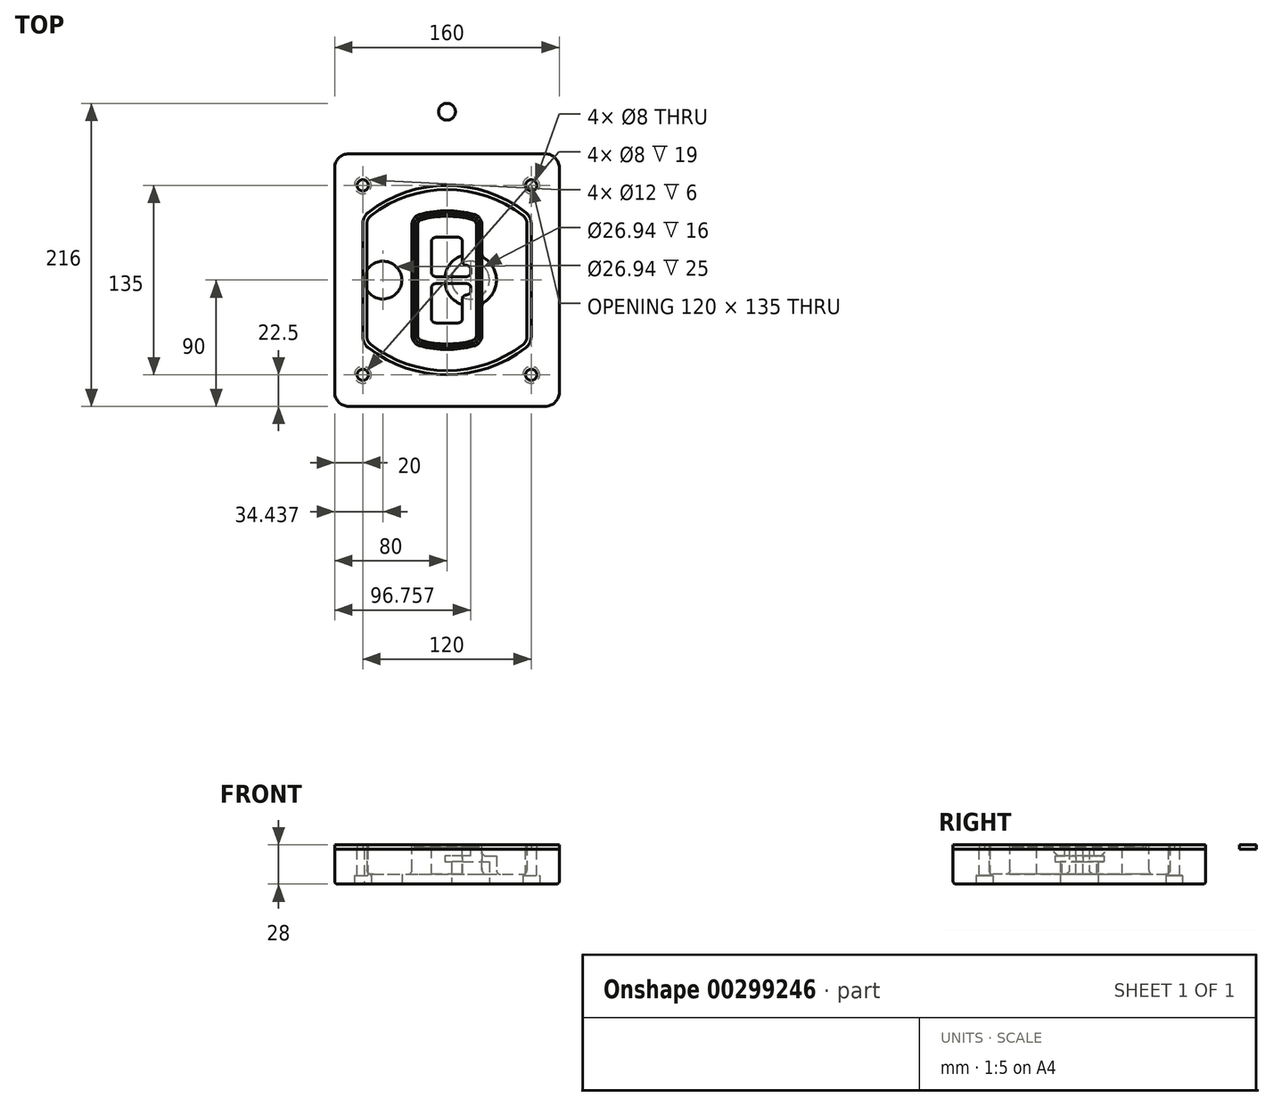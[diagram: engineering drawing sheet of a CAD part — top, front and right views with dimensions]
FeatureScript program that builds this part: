
annotation { "Feature Type Name" : "Feature", "Feature Type Description" : "" }
export const myFeature = defineFeature(function(context is Context, id is Id, definition is map)
    precondition{}
    {
        {
            var Q0;
            Q0=qCreatedBy(makeId("Top.planeOp"),FACE);
            var sketch = newSketch(context, id + "F0", { "sketchPlane" : qUnion([Q0])});
            skPoint(sketch, "E0.rect.middle", {"position": v(0, 0) * mm});
            skLineSegment(sketch, "E1.bottom", {"start": v(-70, -90) * mm, "end": v(70, -90) * mm});
            skLineSegment(sketch, "E1.top", {"start": v(-70, 90) * mm, "end": v(70, 90) * mm});
            skLineSegment(sketch, "E1.left", {"start": v(-80, -80) * mm, "end": v(-80, 80) * mm});
            skLineSegment(sketch, "E1.right", {"start": v(80, -80) * mm, "end": v(80, 80) * mm});
            skLineSegment(sketch, "E2", {"start": v(-80, 90) * mm, "end": v(80, -90) * mm, "construction": true});
            skLineSegment(sketch, "E3", {"start": v(80, 90) * mm, "end": v(-80, -90) * mm, "construction": true});
            skCircle(sketch, "E4", {"center": v(-60, 67.5) * mm, "radius": 4 * mm});
            skCircle(sketch, "E5", {"center": v(60, 67.5) * mm, "radius": 4 * mm});
            skCircle(sketch, "E6", {"center": v(60, -67.5) * mm, "radius": 4 * mm});
            skCircle(sketch, "E7", {"center": v(-60, -67.5) * mm, "radius": 4 * mm});
            skLineSegment(sketch, "E8", {"start": v(-60, 67.5) * mm, "end": v(60, 67.5) * mm, "construction": true});
            skLineSegment(sketch, "E9", {"start": v(60, 67.5) * mm, "end": v(60, -67.5) * mm, "construction": true});
            skLineSegment(sketch, "E10", {"start": v(60, -67.5) * mm, "end": v(-60, -67.5) * mm, "construction": true});
            skLineSegment(sketch, "E11", {"start": v(-60, -67.5) * mm, "end": v(-60, 67.5) * mm, "construction": true});
            skLineSegment(sketch, "E12", {"start": v(-60, 40.3) * mm, "end": v(-60, -40.3) * mm});
            skLineSegment(sketch, "E13", {"start": v(60, 40.3) * mm, "end": v(60, -40.3) * mm});
            skArc(sketch, "E14", {"start": v(56.15, 48.18) * mm, "mid": v(0, 67.5) * mm, "end": v(-56.15, 48.18) * mm});
            skArc(sketch, "E15", {"start": v(-56.15, -48.18) * mm, "mid": v(0, -67.5) * mm, "end": v(56.15, -48.18) * mm});
            skLineSegment(sketch, "E16", {"start": v(-60, 0) * mm, "end": v(60, 0) * mm, "construction": true});
            skPoint(sketch, "E17.visualSharp", {"position": v(-60, -45) * mm});
            skArc(sketch, "E17.filletArc", {"start": v(-60, -40.3) * mm, "mid": v(-58.99, -44.68) * mm, "end": v(-56.15, -48.18) * mm});
            skPoint(sketch, "E18.visualSharp", {"position": v(-60, 45) * mm});
            skArc(sketch, "E18.filletArc", {"start": v(-56.15, 48.18) * mm, "mid": v(-58.99, 44.68) * mm, "end": v(-60, 40.3) * mm});
            skPoint(sketch, "E19.visualSharp", {"position": v(60, 45) * mm});
            skArc(sketch, "E19.filletArc", {"start": v(60, 40.3) * mm, "mid": v(58.99, 44.68) * mm, "end": v(56.15, 48.18) * mm});
            skPoint(sketch, "E20.visualSharp", {"position": v(60, -45) * mm});
            skArc(sketch, "E20.filletArc", {"start": v(56.15, -48.18) * mm, "mid": v(58.99, -44.68) * mm, "end": v(60, -40.3) * mm});
            skPoint(sketch, "E21.visualSharp", {"position": v(-80, 90) * mm});
            skArc(sketch, "E21.filletArc", {"start": v(-70, 90) * mm, "mid": v(-77.07, 87.07) * mm, "end": v(-80, 80) * mm});
            skPoint(sketch, "E22.visualSharp", {"position": v(80, 90) * mm});
            skArc(sketch, "E22.filletArc", {"start": v(80, 80) * mm, "mid": v(77.07, 87.07) * mm, "end": v(70, 90) * mm});
            skPoint(sketch, "E23.visualSharp", {"position": v(80, -90) * mm});
            skArc(sketch, "E23.filletArc", {"start": v(70, -90) * mm, "mid": v(77.07, -87.07) * mm, "end": v(80, -80) * mm});
            skPoint(sketch, "E24.visualSharp", {"position": v(-80, -90) * mm});
            skArc(sketch, "E24.filletArc", {"start": v(-80, -80) * mm, "mid": v(-77.07, -87.07) * mm, "end": v(-70, -90) * mm});
            skArc(sketch, "E25.0", {"start": v(57, 40.3) * mm, "mid": v(56.3, 43.36) * mm, "end": v(54.3, 45.81) * mm});
            skLineSegment(sketch, "E25.1", {"start": v(57, 40.3) * mm, "end": v(57, -40.3) * mm});
            skArc(sketch, "E25.2", {"start": v(54.3, -45.81) * mm, "mid": v(56.3, -43.36) * mm, "end": v(57, -40.3) * mm});
            skArc(sketch, "E25.3", {"start": v(-54.3, -45.81) * mm, "mid": v(0, -64.5) * mm, "end": v(54.3, -45.81) * mm});
            skArc(sketch, "E25.4", {"start": v(-57, -40.3) * mm, "mid": v(-56.3, -43.36) * mm, "end": v(-54.3, -45.81) * mm});
            skArc(sketch, "E25.5", {"start": v(54.3, 45.81) * mm, "mid": v(0, 64.5) * mm, "end": v(-54.3, 45.81) * mm});
            skLineSegment(sketch, "E25.6", {"start": v(-57, 40.3) * mm, "end": v(-57, -40.3) * mm});
            skArc(sketch, "E25.7", {"start": v(-54.3, 45.81) * mm, "mid": v(-56.3, 43.36) * mm, "end": v(-57, 40.3) * mm});
            skArc(sketch, "E26.0", {"start": v(-58.62, 51.33) * mm, "mid": v(-62.58, 46.43) * mm, "end": v(-64, 40.3) * mm});
            skArc(sketch, "E26.1", {"start": v(58.62, 51.33) * mm, "mid": v(0, 71.5) * mm, "end": v(-58.62, 51.33) * mm});
            skArc(sketch, "E26.2", {"start": v(64, 40.3) * mm, "mid": v(62.58, 46.43) * mm, "end": v(58.62, 51.33) * mm});
            skLineSegment(sketch, "E26.3", {"start": v(64, 40.3) * mm, "end": v(64, -40.3) * mm});
            skArc(sketch, "E26.4", {"start": v(58.62, -51.33) * mm, "mid": v(62.58, -46.43) * mm, "end": v(64, -40.3) * mm});
            skLineSegment(sketch, "E26.5", {"start": v(-64, 40.3) * mm, "end": v(-64, -40.3) * mm});
            skArc(sketch, "E26.6", {"start": v(-58.62, -51.33) * mm, "mid": v(0, -71.5) * mm, "end": v(58.62, -51.33) * mm});
            skArc(sketch, "E26.7", {"start": v(-64, -40.3) * mm, "mid": v(-62.58, -46.43) * mm, "end": v(-58.62, -51.33) * mm});
            skSolve(sketch);
        }
        {
            var Q0;
            Q0=makeQuery(id+"F0.imprint","IMPRINT",FACE,{"disambiguationData":[TD([[makeQuery(id+"F0.imprint","IMPRINT",EDGE,{"derivedFrom":sQuery(id+"F0.wireOp",EDGE,"E1.bottom")}),1.0]])]});
            var Q1;
            Q1=makeQuery(id+"F0.imprint","IMPRINT",FACE,{"disambiguationData":[TD([[makeQuery(id+"F0.imprint","IMPRINT",EDGE,{"derivedFrom":sQuery(id+"F0.wireOp",EDGE,"E12")}),1.0]])]});
            var Q2;
            Q2=makeQuery(id+"F0.imprint","IMPRINT",FACE,{"disambiguationData":[TD([[makeQuery(id+"F0.imprint","IMPRINT",EDGE,{"derivedFrom":sQuery(id+"F0.wireOp",EDGE,"E25.0")}),1.0]])]});
            var Q3;
            Q3=makeQuery(id+"F0.imprint","IMPRINT",FACE,{"disambiguationData":[TD([[makeQuery(id+"F0.imprint","IMPRINT",EDGE,{"derivedFrom":sQuery(id+"F0.wireOp",EDGE,"E12")}),-1.0]])]});
            extrude(context, id + "F1", {"entities" : qUnion([Q0, Q1, Q2, Q3]), "oppositeDirection" : true, "depth" : 25 * mm});
        }
        {
            var Q0;
            Q0=makeQuery(id+"F0.imprint","IMPRINT",FACE,{"disambiguationData":[TD([[makeQuery(id+"F0.imprint","IMPRINT",EDGE,{"derivedFrom":sQuery(id+"F0.wireOp",EDGE,"E12")}),1.0]])]});
            extrude(context, id + "F2", {"entities" : qUnion([Q0]), "operationType" : NewBodyOperationType.ADD, "depth" : 3 * mm});
        }
        {
            var Q0;
            Q0=makeQuery(id+"F0.imprint","IMPRINT",FACE,{"disambiguationData":[TD([[makeQuery(id+"F0.imprint","IMPRINT",EDGE,{"derivedFrom":sQuery(id+"F0.wireOp",EDGE,"E25.0")}),1.0]])]});
            extrude(context, id + "F3", {"entities" : qUnion([Q0]), "operationType" : NewBodyOperationType.REMOVE, "oppositeDirection" : true, "depth" : 18 * mm});
        }
        {
            var Q0;
            Q0=makeQuery(id+"F2.opExtrude","CAP_FACE",FACE,{"disambiguationData":[OSD([sQuery(id+"F0.wireOp",EDGE,"E12"),sQuery(id+"F0.wireOp",EDGE,"E13"),sQuery(id+"F0.wireOp",EDGE,"E14"),sQuery(id+"F0.wireOp",EDGE,"E15"),sQuery(id+"F0.wireOp",EDGE,"E17.filletArc"),sQuery(id+"F0.wireOp",EDGE,"E18.filletArc"),sQuery(id+"F0.wireOp",EDGE,"E19.filletArc"),sQuery(id+"F0.wireOp",EDGE,"E20.filletArc"),sQuery(id+"F0.wireOp",EDGE,"E25.0"),sQuery(id+"F0.wireOp",EDGE,"E25.1"),sQuery(id+"F0.wireOp",EDGE,"E25.2"),sQuery(id+"F0.wireOp",EDGE,"E25.3"),sQuery(id+"F0.wireOp",EDGE,"E25.4"),sQuery(id+"F0.wireOp",EDGE,"E25.5"),sQuery(id+"F0.wireOp",EDGE,"E25.6"),sQuery(id+"F0.wireOp",EDGE,"E25.7")])],"isStart":false});
            var sketch = newSketch(context, id + "F4", { "sketchPlane" : qUnion([Q0])});
            skArc(sketch, "E27.0", {"start": v(-19.08, -46.97) * mm, "mid": v(0, -49.5) * mm, "end": v(19.08, -46.97) * mm});
            skArc(sketch, "E28.0", {"start": v(19.08, 46.97) * mm, "mid": v(0, 49.5) * mm, "end": v(-19.08, 46.97) * mm});
            skLineSegment(sketch, "E29", {"start": v(-25, 39.25) * mm, "end": v(-25, -39.25) * mm});
            skLineSegment(sketch, "E30", {"start": v(25, 39.25) * mm, "end": v(25, -39.25) * mm});
            skLineSegment(sketch, "E31", {"start": v(-25, 45.1) * mm, "end": v(25, 45.1) * mm, "construction": true});
            skLineSegment(sketch, "E32", {"start": v(-25, -45.1) * mm, "end": v(25, -45.1) * mm, "construction": true});
            skPoint(sketch, "E33.visualSharp", {"position": v(-25, 45.1) * mm});
            skArc(sketch, "E33.filletArc", {"start": v(-19.08, 46.97) * mm, "mid": v(-23.35, 44.11) * mm, "end": v(-25, 39.25) * mm});
            skPoint(sketch, "E34.visualSharp", {"position": v(25, 45.1) * mm});
            skArc(sketch, "E34.filletArc", {"start": v(25, 39.25) * mm, "mid": v(23.35, 44.11) * mm, "end": v(19.08, 46.97) * mm});
            skPoint(sketch, "E35.visualSharp", {"position": v(25, -45.1) * mm});
            skArc(sketch, "E35.filletArc", {"start": v(19.08, -46.97) * mm, "mid": v(23.35, -44.11) * mm, "end": v(25, -39.25) * mm});
            skPoint(sketch, "E36.visualSharp", {"position": v(-25, -45.1) * mm});
            skArc(sketch, "E36.filletArc", {"start": v(-25, -39.25) * mm, "mid": v(-23.35, -44.11) * mm, "end": v(-19.08, -46.97) * mm});
            skArc(sketch, "E37.0", {"start": v(54.3, 45.81) * mm, "mid": v(0, 64.5) * mm, "end": v(-54.3, 45.81) * mm});
            skArc(sketch, "E37.1", {"start": v(-54.3, 45.81) * mm, "mid": v(-56.3, 43.36) * mm, "end": v(-57, 40.3) * mm});
            skLineSegment(sketch, "E37.2", {"start": v(-57, 40.3) * mm, "end": v(-57, -40.3) * mm});
            skArc(sketch, "E37.3", {"start": v(-57, -40.3) * mm, "mid": v(-56.3, -43.36) * mm, "end": v(-54.3, -45.81) * mm});
            skArc(sketch, "E37.4", {"start": v(-54.3, -45.81) * mm, "mid": v(0, -64.5) * mm, "end": v(54.3, -45.81) * mm});
            skArc(sketch, "E37.5", {"start": v(54.3, -45.81) * mm, "mid": v(56.3, -43.36) * mm, "end": v(57, -40.3) * mm});
            skLineSegment(sketch, "E37.6", {"start": v(57, 40.3) * mm, "end": v(57, -40.3) * mm});
            skArc(sketch, "E37.7", {"start": v(57, 40.3) * mm, "mid": v(56.3, 43.36) * mm, "end": v(54.3, 45.81) * mm});
            skLineSegment(sketch, "E38.0", {"start": v(23, 39.25) * mm, "end": v(23, -39.25) * mm});
            skArc(sketch, "E38.1", {"start": v(18.56, -45.04) * mm, "mid": v(21.76, -42.9) * mm, "end": v(23, -39.25) * mm});
            skArc(sketch, "E38.2", {"start": v(-18.56, -45.04) * mm, "mid": v(0, -47.5) * mm, "end": v(18.56, -45.04) * mm});
            skArc(sketch, "E38.3", {"start": v(-23, -39.25) * mm, "mid": v(-21.76, -42.9) * mm, "end": v(-18.56, -45.04) * mm});
            skLineSegment(sketch, "E38.4", {"start": v(-23, 39.25) * mm, "end": v(-23, -39.25) * mm});
            skArc(sketch, "E38.5", {"start": v(23, 39.25) * mm, "mid": v(21.76, 42.9) * mm, "end": v(18.56, 45.04) * mm});
            skArc(sketch, "E38.6", {"start": v(-18.56, 45.04) * mm, "mid": v(-21.76, 42.9) * mm, "end": v(-23, 39.25) * mm});
            skArc(sketch, "E38.7", {"start": v(18.56, 45.04) * mm, "mid": v(0, 47.5) * mm, "end": v(-18.56, 45.04) * mm});
            skArc(sketch, "E39.0", {"start": v(21, 39.25) * mm, "mid": v(20.18, 41.68) * mm, "end": v(18.04, 43.1) * mm});
            skLineSegment(sketch, "E39.1", {"start": v(21, 39.25) * mm, "end": v(21, -39.25) * mm});
            skArc(sketch, "E39.2", {"start": v(18.04, -43.1) * mm, "mid": v(20.18, -41.68) * mm, "end": v(21, -39.25) * mm});
            skArc(sketch, "E39.3", {"start": v(-18.04, -43.1) * mm, "mid": v(0, -45.5) * mm, "end": v(18.04, -43.1) * mm});
            skArc(sketch, "E39.4", {"start": v(-21, -39.25) * mm, "mid": v(-20.18, -41.68) * mm, "end": v(-18.04, -43.1) * mm});
            skArc(sketch, "E39.5", {"start": v(18.04, 43.1) * mm, "mid": v(0, 45.5) * mm, "end": v(-18.04, 43.1) * mm});
            skLineSegment(sketch, "E39.6", {"start": v(-21, 39.25) * mm, "end": v(-21, -39.25) * mm});
            skArc(sketch, "E39.7", {"start": v(-18.04, 43.1) * mm, "mid": v(-20.18, 41.68) * mm, "end": v(-21, 39.25) * mm});
            skLineSegment(sketch, "E40", {"start": v(-25, 0) * mm, "end": v(25, 0) * mm, "construction": true});
            skLineSegment(sketch, "E41", {"start": v(-11, 5.5) * mm, "end": v(-11, 27.5) * mm});
            skLineSegment(sketch, "E42", {"start": v(-8, 30.5) * mm, "end": v(8, 30.5) * mm});
            skLineSegment(sketch, "E43", {"start": v(11, 27.5) * mm, "end": v(11, 13.5) * mm});
            skLineSegment(sketch, "E44", {"start": v(14, 10.5) * mm, "end": v(14, 10.5) * mm});
            skLineSegment(sketch, "E45", {"start": v(17, 7.5) * mm, "end": v(17, 5.5) * mm});
            skLineSegment(sketch, "E46", {"start": v(14, 2.5) * mm, "end": v(-8, 2.5) * mm});
            skPoint(sketch, "E47.visualSharp", {"position": v(-11, 30.5) * mm});
            skArc(sketch, "E47.filletArc", {"start": v(-8, 30.5) * mm, "mid": v(-10.12, 29.62) * mm, "end": v(-11, 27.5) * mm});
            skPoint(sketch, "E48.visualSharp", {"position": v(11, 30.5) * mm});
            skArc(sketch, "E48.filletArc", {"start": v(11, 27.5) * mm, "mid": v(10.12, 29.62) * mm, "end": v(8, 30.5) * mm});
            skPoint(sketch, "E49.visualSharp", {"position": v(11, 10.5) * mm});
            skArc(sketch, "E49.filletArc", {"start": v(11, 13.5) * mm, "mid": v(11.88, 11.38) * mm, "end": v(14, 10.5) * mm});
            skPoint(sketch, "E50.visualSharp", {"position": v(17, 10.5) * mm});
            skArc(sketch, "E50.filletArc", {"start": v(17, 7.5) * mm, "mid": v(16.12, 9.62) * mm, "end": v(14, 10.5) * mm});
            skPoint(sketch, "E51.visualSharp", {"position": v(17, 2.5) * mm});
            skArc(sketch, "E51.filletArc", {"start": v(14, 2.5) * mm, "mid": v(16.12, 3.38) * mm, "end": v(17, 5.5) * mm});
            skPoint(sketch, "E52.visualSharp", {"position": v(-11, 2.5) * mm});
            skArc(sketch, "E52.filletArc", {"start": v(-11, 5.5) * mm, "mid": v(-10.12, 3.38) * mm, "end": v(-8, 2.5) * mm});
            skLineSegment(sketch, "E53.0.MirrorCS", {"start": v(14, -2.5) * mm, "end": v(-8, -2.5) * mm});
            skArc(sketch, "E54.0.MirrorCS", {"start": v(-11, -5.5) * mm, "mid": v(-10.12, -3.38) * mm, "end": v(-8, -2.5) * mm});
            skLineSegment(sketch, "E55.0.MirrorCS", {"start": v(-11, -5.5) * mm, "end": v(-11, -27.5) * mm});
            skArc(sketch, "E56.0.MirrorCS", {"start": v(-8, -30.5) * mm, "mid": v(-10.12, -29.62) * mm, "end": v(-11, -27.5) * mm});
            skLineSegment(sketch, "E57.0.MirrorCS", {"start": v(-8, -30.5) * mm, "end": v(8, -30.5) * mm});
            skArc(sketch, "E58.0.MirrorCS", {"start": v(11, -27.5) * mm, "mid": v(10.12, -29.62) * mm, "end": v(8, -30.5) * mm});
            skLineSegment(sketch, "E59.0.MirrorCS", {"start": v(11, -27.5) * mm, "end": v(11, -13.5) * mm});
            skArc(sketch, "E60.0.MirrorCS", {"start": v(11, -13.5) * mm, "mid": v(11.88, -11.38) * mm, "end": v(14, -10.5) * mm});
            skArc(sketch, "E61.0.MirrorCS", {"start": v(17, -7.5) * mm, "mid": v(16.12, -9.62) * mm, "end": v(14, -10.5) * mm});
            skLineSegment(sketch, "E62.0.MirrorCS", {"start": v(17, -7.5) * mm, "end": v(17, -5.5) * mm});
            skArc(sketch, "E63.0.MirrorCS", {"start": v(14, -2.5) * mm, "mid": v(16.12, -3.38) * mm, "end": v(17, -5.5) * mm});
            skSolve(sketch);
        }
        {
            var Q0;
            Q0=makeQuery(id+"F4.imprint","IMPRINT",FACE,{"disambiguationData":[TD([[makeQuery(id+"F4.imprint","IMPRINT",EDGE,{"derivedFrom":sQuery(id+"F4.wireOp",EDGE,"E27.0")}),1.0]])]});
            var Q1;
            Q1=makeQuery(id+"F4.imprint","IMPRINT",FACE,{"disambiguationData":[TD([[makeQuery(id+"F4.imprint","IMPRINT",EDGE,{"derivedFrom":sQuery(id+"F4.wireOp",EDGE,"E38.0")}),-1.0]])]});
            var Q2;
            Q2=makeQuery(id+"F4.imprint","IMPRINT",FACE,{"disambiguationData":[TD([[makeQuery(id+"F4.imprint","IMPRINT",EDGE,{"derivedFrom":sQuery(id+"F4.wireOp",EDGE,"E39.0")}),1.0]])]});
            extrude(context, id + "F5", {"entities" : qUnion([Q0, Q1, Q2]), "operationType" : NewBodyOperationType.ADD, "endBound" : BoundingType.UP_TO_NEXT, "oppositeDirection" : true, "depth" : 25 * mm});
        }
        {
            var Q0;
            Q0=makeQuery(id+"F4.imprint","IMPRINT",FACE,{"disambiguationData":[TD([[makeQuery(id+"F4.imprint","IMPRINT",EDGE,{"derivedFrom":sQuery(id+"F4.wireOp",EDGE,"E38.0")}),-1.0]])]});
            extrude(context, id + "F6", {"entities" : qUnion([Q0]), "operationType" : NewBodyOperationType.REMOVE, "oppositeDirection" : true, "depth" : 2 * mm});
        }
        {
            var Q0;
            Q0=makeQuery(id+"F1.opExtrude","CAP_FACE",FACE,{"disambiguationData":[OSD([sQuery(id+"F0.wireOp",EDGE,"E1.bottom"),sQuery(id+"F0.wireOp",EDGE,"E1.top"),sQuery(id+"F0.wireOp",EDGE,"E1.left"),sQuery(id+"F0.wireOp",EDGE,"E1.right"),sQuery(id+"F0.wireOp",EDGE,"E4"),sQuery(id+"F0.wireOp",EDGE,"E5"),sQuery(id+"F0.wireOp",EDGE,"E6"),sQuery(id+"F0.wireOp",EDGE,"E7"),sQuery(id+"F0.wireOp",EDGE,"E21.filletArc"),sQuery(id+"F0.wireOp",EDGE,"E22.filletArc"),sQuery(id+"F0.wireOp",EDGE,"E23.filletArc"),sQuery(id+"F0.wireOp",EDGE,"E24.filletArc")])],"isStart":false});
            var sketch = newSketch(context, id + "F7", { "sketchPlane" : qUnion([Q0])});
            skCircle(sketch, "E64", {"center": v(16.76, 0) * mm, "radius": 13.47 * mm});
            skCircle(sketch, "E65", {"center": v(-45.56, 0) * mm, "radius": 13.47 * mm});
            skLineSegment(sketch, "E66", {"start": v(80, 0) * mm, "end": v(-80, 0) * mm});
            skCircle(sketch, "E67", {"center": v(16.76, 0) * mm, "radius": 18.47 * mm});
            skCircle(sketch, "E68", {"center": v(60, -67.5) * mm, "radius": 6 * mm});
            skCircle(sketch, "E69", {"center": v(-60, -67.5) * mm, "radius": 6 * mm});
            skCircle(sketch, "E70", {"center": v(-60, 67.5) * mm, "radius": 6 * mm});
            skCircle(sketch, "E71", {"center": v(60, 67.5) * mm, "radius": 6 * mm});
            skSolve(sketch);
        }
        {
            var Q0;
            {var subQ1=sQuery(id+"F7.wireOp",EDGE,"E66");var subQ4=sQuery(id+"F7.wireOp",EDGE,"E64");var subQ6=makeQuery(id+"F7.imprint","INTERSECT",VERTEX,{"disambiguationData":[OD(0.0)],"derivedFrom":[subQ4,subQ1]});Q0=makeQuery(id+"F7.imprint","IMPRINT",FACE,{"disambiguationData":[TD([[makeQuery(id+"F7.imprint","IMPRINT",EDGE,{"disambiguationData":[TD([[subQ6,-1.0]])],"derivedFrom":subQ4}),-1.0]])]});}
            var Q1;
            {var subQ0=sQuery(id+"F7.wireOp",EDGE,"E66");var subQ1=sQuery(id+"F7.wireOp",EDGE,"E64");var subQ3=makeQuery(id+"F7.imprint","INTERSECT",VERTEX,{"disambiguationData":[OD(0.0)],"derivedFrom":[subQ1,subQ0]});Q1=makeQuery(id+"F7.imprint","IMPRINT",FACE,{"disambiguationData":[TD([[makeQuery(id+"F7.imprint","IMPRINT",EDGE,{"disambiguationData":[TD([[subQ3,-1.0]])],"derivedFrom":subQ1}),1.0]])]});}
            var Q2;
            {var subQ0=sQuery(id+"F7.wireOp",EDGE,"E66");var subQ1=sQuery(id+"F7.wireOp",EDGE,"E64");var subQ3=makeQuery(id+"F7.imprint","INTERSECT",VERTEX,{"disambiguationData":[OD(0.0)],"derivedFrom":[subQ1,subQ0]});Q2=makeQuery(id+"F7.imprint","IMPRINT",FACE,{"disambiguationData":[TD([[makeQuery(id+"F7.imprint","IMPRINT",EDGE,{"disambiguationData":[TD([[subQ3,1.0]])],"derivedFrom":subQ1}),1.0]])]});}
            var Q3;
            {var subQ1=sQuery(id+"F7.wireOp",EDGE,"E66");var subQ4=sQuery(id+"F7.wireOp",EDGE,"E64");var subQ6=makeQuery(id+"F7.imprint","INTERSECT",VERTEX,{"disambiguationData":[OD(0.0)],"derivedFrom":[subQ4,subQ1]});Q3=makeQuery(id+"F7.imprint","IMPRINT",FACE,{"disambiguationData":[TD([[makeQuery(id+"F7.imprint","IMPRINT",EDGE,{"disambiguationData":[TD([[subQ6,1.0]])],"derivedFrom":subQ4}),-1.0]])]});}
            extrude(context, id + "F8", {"entities" : qUnion([Q0, Q1, Q2, Q3]), "operationType" : NewBodyOperationType.ADD, "oppositeDirection" : true, "depth" : 20 * mm});
        }
        {
            var Q0;
            {var subQ0=sQuery(id+"F7.wireOp",EDGE,"E66");var subQ1=sQuery(id+"F7.wireOp",EDGE,"E64");var subQ3=makeQuery(id+"F7.imprint","INTERSECT",VERTEX,{"disambiguationData":[OD(0.0)],"derivedFrom":[subQ1,subQ0]});Q0=makeQuery(id+"F7.imprint","IMPRINT",FACE,{"disambiguationData":[TD([[makeQuery(id+"F7.imprint","IMPRINT",EDGE,{"disambiguationData":[TD([[subQ3,-1.0]])],"derivedFrom":subQ1}),1.0]])]});}
            var Q1;
            {var subQ0=sQuery(id+"F7.wireOp",EDGE,"E66");var subQ1=sQuery(id+"F7.wireOp",EDGE,"E64");var subQ3=makeQuery(id+"F7.imprint","INTERSECT",VERTEX,{"disambiguationData":[OD(0.0)],"derivedFrom":[subQ1,subQ0]});Q1=makeQuery(id+"F7.imprint","IMPRINT",FACE,{"disambiguationData":[TD([[makeQuery(id+"F7.imprint","IMPRINT",EDGE,{"disambiguationData":[TD([[subQ3,1.0]])],"derivedFrom":subQ1}),1.0]])]});}
            extrude(context, id + "F9", {"entities" : qUnion([Q0, Q1]), "operationType" : NewBodyOperationType.REMOVE, "oppositeDirection" : true, "depth" : 16 * mm});
        }
        {
            var Q0;
            {var subQ0=sQuery(id+"F7.wireOp",EDGE,"E66");var subQ1=sQuery(id+"F7.wireOp",EDGE,"E65");var subQ3=makeQuery(id+"F7.imprint","INTERSECT",VERTEX,{"disambiguationData":[OD(0.0)],"derivedFrom":[subQ1,subQ0]});Q0=makeQuery(id+"F7.imprint","IMPRINT",FACE,{"disambiguationData":[TD([[makeQuery(id+"F7.imprint","IMPRINT",EDGE,{"disambiguationData":[TD([[subQ3,-1.0]])],"derivedFrom":subQ1}),1.0]])]});}
            var Q1;
            {var subQ0=sQuery(id+"F7.wireOp",EDGE,"E66");var subQ1=sQuery(id+"F7.wireOp",EDGE,"E65");var subQ3=makeQuery(id+"F7.imprint","INTERSECT",VERTEX,{"disambiguationData":[OD(0.0)],"derivedFrom":[subQ1,subQ0]});Q1=makeQuery(id+"F7.imprint","IMPRINT",FACE,{"disambiguationData":[TD([[makeQuery(id+"F7.imprint","IMPRINT",EDGE,{"disambiguationData":[TD([[subQ3,1.0]])],"derivedFrom":subQ1}),1.0]])]});}
            extrude(context, id + "F10", {"entities" : qUnion([Q0, Q1]), "operationType" : NewBodyOperationType.REMOVE, "oppositeDirection" : true, "depth" : 25 * mm});
        }
        {
            var Q0;
            Q0=makeQuery(id+"F7.imprint","IMPRINT",FACE,{"disambiguationData":[TD([[makeQuery(id+"F7.imprint","IMPRINT",EDGE,{"derivedFrom":sQuery(id+"F7.wireOp",EDGE,"E68")}),1.0]])]});
            var Q1;
            Q1=makeQuery(id+"F7.imprint","IMPRINT",FACE,{"disambiguationData":[TD([[makeQuery(id+"F7.imprint","IMPRINT",EDGE,{"derivedFrom":makeQuery(id+"F1.opExtrude","CAP_EDGE",EDGE,{"disambiguationData":[OSD([sQuery(id+"F0.wireOp",EDGE,"E5")])],"isStart":false})}),-1.0]])]});
            var Q2;
            Q2=makeQuery(id+"F7.imprint","IMPRINT",FACE,{"disambiguationData":[TD([[makeQuery(id+"F7.imprint","IMPRINT",EDGE,{"derivedFrom":sQuery(id+"F7.wireOp",EDGE,"E69")}),1.0]])]});
            var Q3;
            Q3=makeQuery(id+"F7.imprint","IMPRINT",FACE,{"disambiguationData":[TD([[makeQuery(id+"F7.imprint","IMPRINT",EDGE,{"derivedFrom":makeQuery(id+"F1.opExtrude","CAP_EDGE",EDGE,{"disambiguationData":[OSD([sQuery(id+"F0.wireOp",EDGE,"E4")])],"isStart":false})}),-1.0]])]});
            var Q4;
            Q4=makeQuery(id+"F7.imprint","IMPRINT",FACE,{"disambiguationData":[TD([[makeQuery(id+"F7.imprint","IMPRINT",EDGE,{"derivedFrom":sQuery(id+"F7.wireOp",EDGE,"E70")}),1.0]])]});
            var Q5;
            Q5=makeQuery(id+"F7.imprint","IMPRINT",FACE,{"disambiguationData":[TD([[makeQuery(id+"F7.imprint","IMPRINT",EDGE,{"derivedFrom":makeQuery(id+"F1.opExtrude","CAP_EDGE",EDGE,{"disambiguationData":[OSD([sQuery(id+"F0.wireOp",EDGE,"E7")])],"isStart":false})}),-1.0]])]});
            var Q6;
            Q6=makeQuery(id+"F7.imprint","IMPRINT",FACE,{"disambiguationData":[TD([[makeQuery(id+"F7.imprint","IMPRINT",EDGE,{"derivedFrom":sQuery(id+"F7.wireOp",EDGE,"E71")}),1.0]])]});
            var Q7;
            Q7=makeQuery(id+"F7.imprint","IMPRINT",FACE,{"disambiguationData":[TD([[makeQuery(id+"F7.imprint","IMPRINT",EDGE,{"derivedFrom":makeQuery(id+"F1.opExtrude","CAP_EDGE",EDGE,{"disambiguationData":[OSD([sQuery(id+"F0.wireOp",EDGE,"E6")])],"isStart":false})}),-1.0]])]});
            extrude(context, id + "F11", {"entities" : qUnion([Q0, Q1, Q2, Q3, Q4, Q5, Q6, Q7]), "operationType" : NewBodyOperationType.REMOVE, "oppositeDirection" : true, "depth" : 6 * mm});
        }
        {
            var Q0;
            Q0=makeQuery(id+"F9.boolean.opBoolean","COPY",FACE,{"derivedFrom":makeQuery(id+"F9.opExtrude","CAP_FACE",FACE,{"disambiguationData":[OSD([sQuery(id+"F7.wireOp",EDGE,"E64")])],"isStart":false})});
            var sketch = newSketch(context, id + "F12", { "sketchPlane" : qUnion([Q0])});
            skArc(sketch, "E72.0", {"start": v(11, 17.55) * mm, "mid": v(2.57, 11.82) * mm, "end": v(-1.54, 2.5) * mm});
            skArc(sketch, "E72.1", {"start": v(-1.54, -2.5) * mm, "mid": v(2.57, -11.82) * mm, "end": v(11, -17.55) * mm});
            skLineSegment(sketch, "E73", {"start": v(-1.54, -2.5) * mm, "end": v(14, -2.5) * mm});
            skLineSegment(sketch, "E74.0", {"start": v(14, 2.5) * mm, "end": v(-1.54, 2.5) * mm});
            skArc(sketch, "E74.1", {"start": v(14, 2.5) * mm, "mid": v(16.12, 3.38) * mm, "end": v(17, 5.5) * mm});
            skLineSegment(sketch, "E74.2", {"start": v(17, 7.5) * mm, "end": v(17, 5.5) * mm});
            skArc(sketch, "E74.3", {"start": v(17, 7.5) * mm, "mid": v(16.12, 9.62) * mm, "end": v(14, 10.5) * mm});
            skArc(sketch, "E74.4", {"start": v(11, 13.5) * mm, "mid": v(11.88, 11.38) * mm, "end": v(14, 10.5) * mm});
            skLineSegment(sketch, "E74.5", {"start": v(11, 17.55) * mm, "end": v(11, 13.5) * mm});
            skLineSegment(sketch, "E74.7", {"start": v(14, -2.5) * mm, "end": v(-1.54, -2.5) * mm});
            skArc(sketch, "E74.8", {"start": v(14, -2.5) * mm, "mid": v(16.12, -3.38) * mm, "end": v(17, -5.5) * mm});
            skLineSegment(sketch, "E74.9", {"start": v(17, -7.5) * mm, "end": v(17, -5.5) * mm});
            skArc(sketch, "E74.10", {"start": v(17, -7.5) * mm, "mid": v(16.12, -9.62) * mm, "end": v(14, -10.5) * mm});
            skArc(sketch, "E74.11", {"start": v(11, -13.5) * mm, "mid": v(11.88, -11.38) * mm, "end": v(14, -10.5) * mm});
            skLineSegment(sketch, "E74.12", {"start": v(11, -17.55) * mm, "end": v(11, -13.5) * mm});
            skPoint(sketch, "E75.orphan", {"position": v(11, -27.5) * mm});
            skPoint(sketch, "E76.orphan", {"position": v(-8, -2.5) * mm});
            skPoint(sketch, "E77.orphan", {"position": v(-8, 2.5) * mm});
            skPoint(sketch, "E78.orphan", {"position": v(11, 27.5) * mm});
            skSolve(sketch);
        }
        {
            var Q0;
            {var subQ7=sQuery(id+"F12.wireOp",EDGE,"E72.0");var subQ14=sQuery(id+"F12.wireOp",EDGE,"E72.1");var subQ16=sQuery(id+"F12.wireOp",EDGE,"E74.1");var subQ18=sQuery(id+"F12.wireOp",EDGE,"E74.8");Q0=qUnion([makeQuery(id+"F12.imprint","IMPRINT",FACE,{"disambiguationData":[TD([[makeQuery(id+"F12.imprint","IMPRINT",EDGE,{"derivedFrom":subQ7}),1.0]])]}),makeQuery(id+"F12.imprint","IMPRINT",FACE,{"disambiguationData":[TD([[makeQuery(id+"F12.imprint","IMPRINT",EDGE,{"derivedFrom":subQ14}),1.0]])]}),makeQuery(id+"F12.imprint","IMPRINT",FACE,{"disambiguationData":[TD([[makeQuery(id+"F12.imprint","IMPRINT",EDGE,{"derivedFrom":subQ16}),1.0]])]}),makeQuery(id+"F12.imprint","IMPRINT",FACE,{"disambiguationData":[TD([[makeQuery(id+"F12.imprint","IMPRINT",EDGE,{"derivedFrom":subQ18}),-1.0]])]})]);}
            var Q1;
            Q1=makeQuery(id+"F5.boolean.opBoolean","SPLIT",FACE,{"disambiguationData":[TD([makeQuery(id+"F5.opExtrude","SWEPT_FACE",FACE,{"disambiguationData":[OSD([sQuery(id+"F4.wireOp",EDGE,"E41")])]})])],"derivedFrom":makeQuery(id+"F3.boolean.opBoolean","COPY",FACE,{"derivedFrom":makeQuery(id+"F3.opExtrude","CAP_FACE",FACE,{"disambiguationData":[OSD([sQuery(id+"F0.wireOp",EDGE,"E25.0"),sQuery(id+"F0.wireOp",EDGE,"E25.1"),sQuery(id+"F0.wireOp",EDGE,"E25.2"),sQuery(id+"F0.wireOp",EDGE,"E25.3"),sQuery(id+"F0.wireOp",EDGE,"E25.4"),sQuery(id+"F0.wireOp",EDGE,"E25.5"),sQuery(id+"F0.wireOp",EDGE,"E25.6"),sQuery(id+"F0.wireOp",EDGE,"E25.7")])],"isStart":false})})});
            extrude(context, id + "F13", {"entities" : qUnion([Q0]), "operationType" : NewBodyOperationType.REMOVE, "endBound" : BoundingType.UP_TO_SURFACE, "endBoundEntityFace" : qUnion([Q1]), "depth" : 25 * mm});
        }
        {
            var Q0;
            Q0=makeQuery(id+"F3.boolean.opBoolean","COPY",EDGE,{"derivedFrom":makeQuery(id+"F3.opExtrude","CAP_EDGE",EDGE,{"disambiguationData":[OSD([sQuery(id+"F0.wireOp",EDGE,"E25.6")])],"isStart":false})});
            var Q1;
            Q1=makeQuery(id+"F8.boolean.opBoolean","INTERSECT",EDGE,{"derivedFrom":[makeQuery(id+"F5.opExtrude","SWEPT_FACE",FACE,{"disambiguationData":[OSD([sQuery(id+"F4.wireOp",EDGE,"E30")])]}),makeQuery(id+"F8.opExtrude","CAP_FACE",FACE,{"disambiguationData":[OSD([sQuery(id+"F7.wireOp",EDGE,"E67")])],"isStart":false})]});
            var Q2;
            Q2=makeQuery(id+"F8.boolean.opBoolean","INTERSECT",EDGE,{"disambiguationData":[OD(1.0)],"derivedFrom":[makeQuery(id+"F5.opExtrude","SWEPT_FACE",FACE,{"disambiguationData":[OSD([sQuery(id+"F4.wireOp",EDGE,"E30")])]}),makeQuery(id+"F8.opExtrude","SWEPT_FACE",FACE,{"disambiguationData":[OSD([sQuery(id+"F7.wireOp",EDGE,"E67")])]})]});
            var Q3;
            {var subQ0=sQuery(id+"F4.wireOp",EDGE,"E30");Q3=makeQuery(id+"F8.boolean.opBoolean","SPLIT",EDGE,{"disambiguationData":[TD([makeQuery(id+"F5.opExtrude","SWEPT_FACE",FACE,{"disambiguationData":[OSD([sQuery(id+"F4.wireOp",EDGE,"E35.filletArc")])]})])],"derivedFrom":makeQuery(id+"F5.opExtrude","CAP_EDGE",EDGE,{"disambiguationData":[OSD([subQ0])],"isStart":false})});}
            var Q4;
            {var subQ0=sQuery(id+"F0.wireOp",EDGE,"E25.7");var subQ1=sQuery(id+"F0.wireOp",EDGE,"E25.1");var subQ2=sQuery(id+"F0.wireOp",EDGE,"E25.6");var subQ3=sQuery(id+"F0.wireOp",EDGE,"E25.5");var subQ4=sQuery(id+"F0.wireOp",EDGE,"E25.4");var subQ5=sQuery(id+"F0.wireOp",EDGE,"E25.0");var subQ6=sQuery(id+"F0.wireOp",EDGE,"E25.2");var subQ7=sQuery(id+"F0.wireOp",EDGE,"E25.3");Q4=makeQuery(id+"F8.boolean.opBoolean","INTERSECT",EDGE,{"derivedFrom":[makeQuery(id+"F5.boolean.opBoolean","SPLIT",FACE,{"disambiguationData":[TD([makeQuery(id+"F2.opExtrude","SWEPT_FACE",FACE,{"disambiguationData":[OSD([subQ5])]})])],"derivedFrom":makeQuery(id+"F3.boolean.opBoolean","COPY",FACE,{"derivedFrom":makeQuery(id+"F3.opExtrude","CAP_FACE",FACE,{"disambiguationData":[OSD([subQ5,subQ1,subQ6,subQ7,subQ4,subQ3,subQ2,subQ0])],"isStart":false})})}),makeQuery(id+"F8.opExtrude","SWEPT_FACE",FACE,{"disambiguationData":[OSD([sQuery(id+"F7.wireOp",EDGE,"E67")])]})]});}
            var Q5;
            Q5=makeQuery(id+"F8.boolean.opBoolean","INTERSECT",EDGE,{"disambiguationData":[OD(0.0)],"derivedFrom":[makeQuery(id+"F5.opExtrude","SWEPT_FACE",FACE,{"disambiguationData":[OSD([sQuery(id+"F4.wireOp",EDGE,"E30")])]}),makeQuery(id+"F8.opExtrude","SWEPT_FACE",FACE,{"disambiguationData":[OSD([sQuery(id+"F7.wireOp",EDGE,"E67")])]})]});
            fillet(context, id + "F14", {"entities" : qUnion([Q0, Q1, Q2, Q3, Q4, Q5]), "radius" : 3 * mm, "tangentPropagation" : true, "allowEdgeOverflow" : false});
        }
        {
            var Q0;
            Q0=makeQuery(id+"F1.opExtrude","CAP_EDGE",EDGE,{"disambiguationData":[OSD([sQuery(id+"F0.wireOp",EDGE,"E1.bottom")])],"isStart":false});
            fillet(context, id + "F15", {"entities" : qUnion([Q0]), "radius" : 2 * mm, "tangentPropagation" : true, "allowEdgeOverflow" : false});
        }
        {
            var Q0;
            {var subQ0=sQuery(id+"F0.wireOp",EDGE,"E21.filletArc");var subQ1=sQuery(id+"F0.wireOp",EDGE,"E7");var subQ2=sQuery(id+"F0.wireOp",EDGE,"E6");var subQ3=sQuery(id+"F0.wireOp",EDGE,"E5");var subQ4=sQuery(id+"F0.wireOp",EDGE,"E4");var subQ5=sQuery(id+"F0.wireOp",EDGE,"E22.filletArc");var subQ6=sQuery(id+"F0.wireOp",EDGE,"E1.bottom");var subQ7=sQuery(id+"F0.wireOp",EDGE,"E1.right");var subQ8=sQuery(id+"F0.wireOp",EDGE,"E1.top");var subQ9=sQuery(id+"F0.wireOp",EDGE,"E1.left");var subQ10=sQuery(id+"F0.wireOp",EDGE,"E23.filletArc");var subQ11=sQuery(id+"F0.wireOp",EDGE,"E24.filletArc");Q0=makeQuery(id+"F2.boolean.opBoolean","SPLIT",FACE,{"disambiguationData":[TD([makeQuery(id+"F1.opExtrude","SWEPT_FACE",FACE,{"disambiguationData":[OSD([subQ6])]})])],"derivedFrom":makeQuery(id+"F1.opExtrude","CAP_FACE",FACE,{"disambiguationData":[OSD([subQ6,subQ8,subQ9,subQ7,subQ4,subQ3,subQ2,subQ1,subQ0,subQ5,subQ10,subQ11])],"isStart":true})});}
            var sketch = newSketch(context, id + "F16", { "sketchPlane" : qUnion([Q0])});
            skLineSegment(sketch, "E79", {"start": v(0, 90) * mm, "end": v(0, 90) * mm});
            skLineSegment(sketch, "E80", {"start": v(0, 90) * mm, "end": v(0, 120) * mm, "construction": true});
            skCircle(sketch, "E81", {"center": v(0, 120) * mm, "radius": 6 * mm});
            skArc(sketch, "E82", {"start": v(15, 120) * mm, "mid": v(0, 135) * mm, "end": v(-15, 120) * mm});
            skLineSegment(sketch, "E83", {"start": v(-15, 120) * mm, "end": v(-15, 108) * mm});
            skLineSegment(sketch, "E84", {"start": v(-15, 108) * mm, "end": v(-33, 90) * mm});
            skLineSegment(sketch, "E85", {"start": v(15, 120) * mm, "end": v(15, 108) * mm});
            skLineSegment(sketch, "E86", {"start": v(15, 108) * mm, "end": v(33, 90) * mm});
            skLineSegment(sketch, "E87", {"start": v(-80, 0) * mm, "end": v(80, 0) * mm, "construction": true});
            skLineSegment(sketch, "E88.MirrorCS", {"start": v(15, -108) * mm, "end": v(33, -90) * mm});
            skArc(sketch, "E89.MirrorCS", {"start": v(15, -120) * mm, "mid": v(0, -135) * mm, "end": v(-15, -120) * mm});
            skLineSegment(sketch, "E90.MirrorCS", {"start": v(-15, -120) * mm, "end": v(-15, -108) * mm});
            skLineSegment(sketch, "E91.MirrorCS", {"start": v(-15, -108) * mm, "end": v(-33, -90) * mm});
            skLineSegment(sketch, "E92.MirrorCS", {"start": v(15, -120) * mm, "end": v(15, -108) * mm});
            skCircle(sketch, "E93.MirrorC", {"center": v(0, -120) * mm, "radius": 6 * mm});
            skLineSegment(sketch, "E94.MirrorCS", {"start": v(0, -90) * mm, "end": v(0, -120) * mm, "construction": true});
            skSolve(sketch);
        }
        {
            var Q0;
            Q0=makeQuery(id+"F16.imprint","IMPRINT",FACE,{"disambiguationData":[TD([[makeQuery(id+"F16.imprint","IMPRINT",EDGE,{"derivedFrom":sQuery(id+"F16.wireOp",EDGE,"E81")}),1.0]])]});
            var Q1;
            Q1=makeQuery(id+"F16.imprint","IMPRINT",FACE,{"disambiguationData":[TD([[makeQuery(id+"F16.imprint","IMPRINT",EDGE,{"derivedFrom":sQuery(id+"F16.wireOp",EDGE,"E89.MirrorCS")}),-1.0]])]});
            var Q2;
            Q2=makeQuery(id+"F16.imprint","IMPRINT",FACE,{"disambiguationData":[TD([[makeQuery(id+"F16.imprint","IMPRINT",EDGE,{"derivedFrom":makeQuery(id+"F1.opExtrude","CAP_EDGE",EDGE,{"disambiguationData":[OSD([sQuery(id+"F0.wireOp",EDGE,"E1.left")])],"isStart":true})}),-1.0]])]});
            var Q3;
            Q3=makeQuery(id+"F2.opExtrude","CAP_FACE",FACE,{"disambiguationData":[OSD([sQuery(id+"F0.wireOp",EDGE,"E12"),sQuery(id+"F0.wireOp",EDGE,"E13"),sQuery(id+"F0.wireOp",EDGE,"E14"),sQuery(id+"F0.wireOp",EDGE,"E15"),sQuery(id+"F0.wireOp",EDGE,"E17.filletArc"),sQuery(id+"F0.wireOp",EDGE,"E18.filletArc"),sQuery(id+"F0.wireOp",EDGE,"E19.filletArc"),sQuery(id+"F0.wireOp",EDGE,"E20.filletArc"),sQuery(id+"F0.wireOp",EDGE,"E25.0"),sQuery(id+"F0.wireOp",EDGE,"E25.1"),sQuery(id+"F0.wireOp",EDGE,"E25.2"),sQuery(id+"F0.wireOp",EDGE,"E25.3"),sQuery(id+"F0.wireOp",EDGE,"E25.4"),sQuery(id+"F0.wireOp",EDGE,"E25.5"),sQuery(id+"F0.wireOp",EDGE,"E25.6"),sQuery(id+"F0.wireOp",EDGE,"E25.7")])],"isStart":false});
            extrude(context, id + "F17", {"entities" : qUnion([Q0, Q1, Q2]), "endBound" : BoundingType.UP_TO_SURFACE, "endBoundEntityFace" : qUnion([Q3]), "depth" : 25 * mm});
        }
    });
